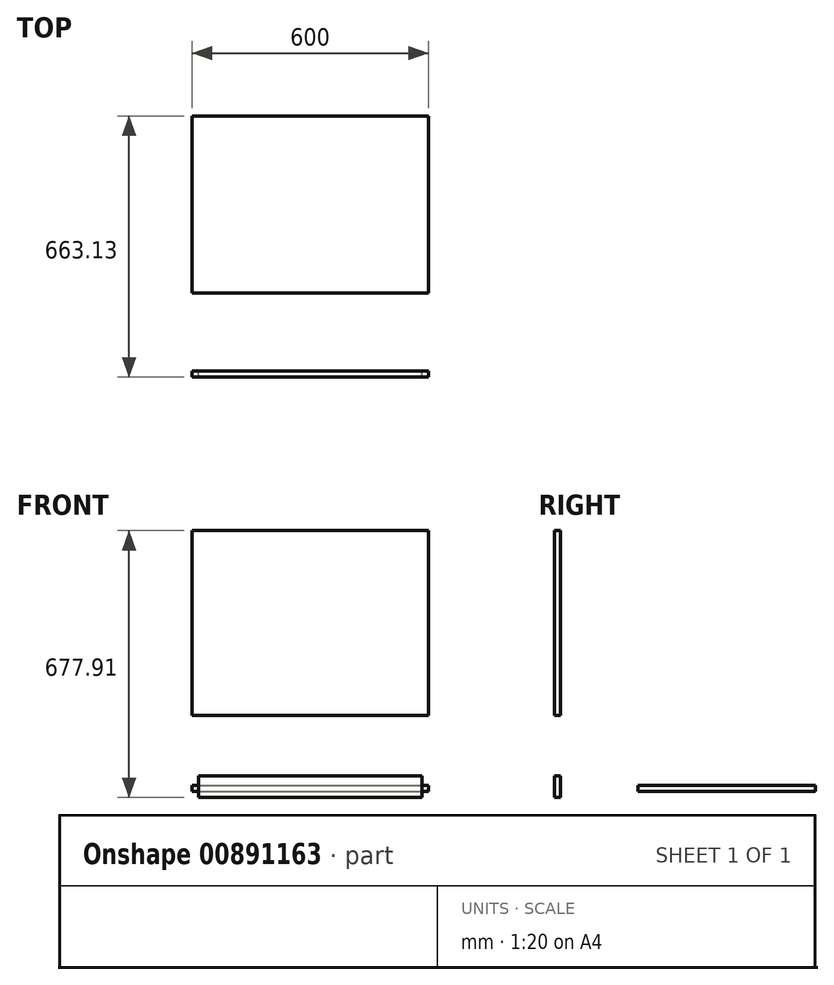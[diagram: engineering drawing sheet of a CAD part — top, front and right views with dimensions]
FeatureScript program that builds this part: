
annotation { "Feature Type Name" : "Feature", "Feature Type Description" : "" }
export const myFeature = defineFeature(function(context is Context, id is Id, definition is map)
    precondition{}
    {
        {
            assignVariable(context, id + "F0", {"name" : "GrosorTableros", "anyValue" : 16});
        }
        {
            var Q0;
            Q0=qCreatedBy(makeId("Front.planeOp"),FACE);
            var sketch = newSketch(context, id + "F1", { "sketchPlane" : qUnion([Q0])});
            skLineSegment(sketch, "E0.bottom", {"start": v(-284, 39.98) * mm, "end": v(284, 39.98) * mm});
            skLineSegment(sketch, "E0.top", {"start": v(-284, -15.02) * mm, "end": v(284, -15.02) * mm});
            skLineSegment(sketch, "E0.left", {"start": v(-284, 39.98) * mm, "end": v(-284, -15.02) * mm});
            skLineSegment(sketch, "E0.right", {"start": v(284, 39.98) * mm, "end": v(284, -15.02) * mm});
            skSolve(sketch);
        }
        {
            var Q0;
            Q0=makeQuery(id+"F1.imprint","IMPRINT",FACE,{"disambiguationData":[TD([[makeQuery(id+"F1.imprint","IMPRINT",EDGE,{"derivedFrom":sQuery(id+"F1.wireOp",EDGE,"E0.bottom")}),-1.0]])]});
            extrude(context, id + "F2", {"entities" : qUnion([Q0]), "depth" : (getVariable(context, 'GrosorTableros')) * mm, "offsetDistance" : 25 * mm});
        }
        {
            var Q0;
            Q0=qCreatedBy(makeId("Top.planeOp"),FACE);
            var sketch = newSketch(context, id + "F3", { "sketchPlane" : qUnion([Q0])});
            skLineSegment(sketch, "E1.bottom", {"start": v(-300, 647.13) * mm, "end": v(300, 647.13) * mm});
            skLineSegment(sketch, "E1.top", {"start": v(-300, 197.13) * mm, "end": v(300, 197.13) * mm});
            skLineSegment(sketch, "E1.left", {"start": v(-300, 647.13) * mm, "end": v(-300, 197.13) * mm});
            skLineSegment(sketch, "E1.right", {"start": v(300, 647.13) * mm, "end": v(300, 197.13) * mm});
            skSolve(sketch);
        }
        {
            var Q0;
            Q0=makeQuery(id+"F3.imprint","IMPRINT",FACE,{"disambiguationData":[TD([[makeQuery(id+"F3.imprint","IMPRINT",EDGE,{"derivedFrom":sQuery(id+"F3.wireOp",EDGE,"E1.bottom")}),-1.0]])]});
            extrude(context, id + "F4", {"entities" : qUnion([Q0]), "operationType" : NewBodyOperationType.ADD, "depth" : (getVariable(context, 'GrosorTableros')) * mm, "offsetDistance" : 25 * mm});
        }
        {
            var Q0;
            Q0=qCreatedBy(makeId("Front.planeOp"),FACE);
            var sketch = newSketch(context, id + "F5", { "sketchPlane" : qUnion([Q0])});
            skLineSegment(sketch, "E2.bottom", {"start": v(-300, 662.89) * mm, "end": v(300, 662.89) * mm});
            skLineSegment(sketch, "E2.top", {"start": v(-300, 192.89) * mm, "end": v(300, 192.89) * mm});
            skLineSegment(sketch, "E2.left", {"start": v(-300, 662.89) * mm, "end": v(-300, 192.89) * mm});
            skLineSegment(sketch, "E2.right", {"start": v(300, 662.89) * mm, "end": v(300, 192.89) * mm});
            skSolve(sketch);
        }
        {
            var Q0;
            Q0=makeQuery(id+"F5.imprint","IMPRINT",FACE,{"disambiguationData":[TD([[makeQuery(id+"F5.imprint","IMPRINT",EDGE,{"derivedFrom":sQuery(id+"F5.wireOp",EDGE,"E2.bottom")}),-1.0]])]});
            extrude(context, id + "F6", {"entities" : qUnion([Q0]), "operationType" : NewBodyOperationType.ADD, "depth" : (getVariable(context, 'GrosorTableros')) * mm, "offsetDistance" : 25 * mm});
        }
    });
